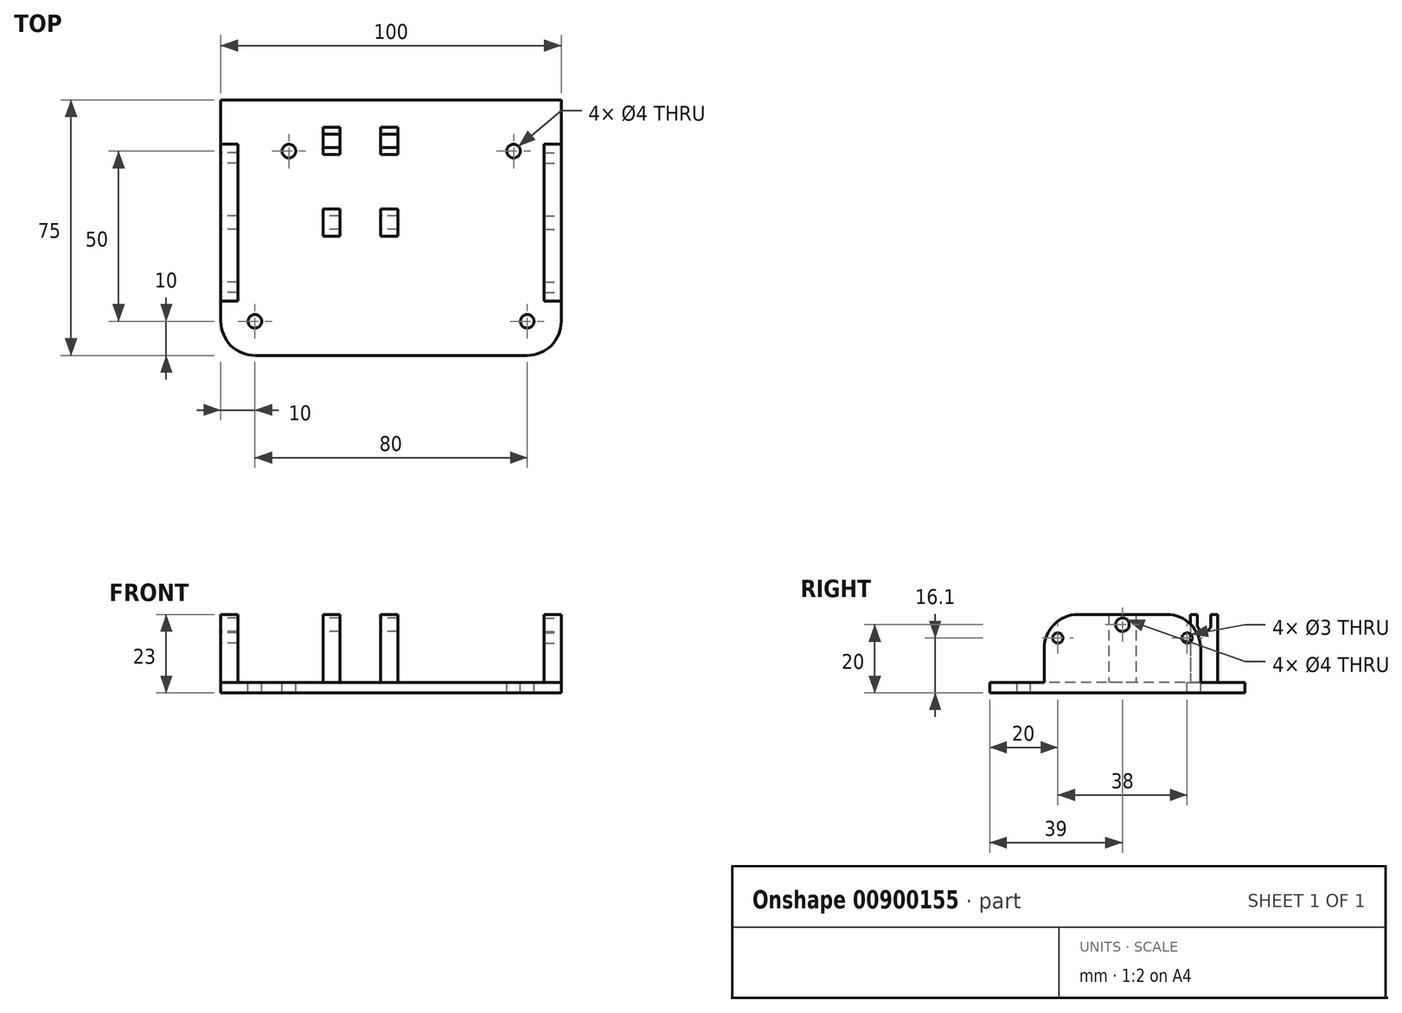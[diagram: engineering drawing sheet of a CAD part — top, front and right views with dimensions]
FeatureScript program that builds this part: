
annotation { "Feature Type Name" : "Feature", "Feature Type Description" : "" }
export const myFeature = defineFeature(function(context is Context, id is Id, definition is map)
    precondition{}
    {
        {
            var Q0;
            Q0=qCreatedBy(makeId("Top.planeOp"),FACE);
            var sketch = newSketch(context, id + "F0", { "sketchPlane" : qUnion([Q0])});
            skLineSegment(sketch, "E0.bottom", {"start": v(50, 37.5) * mm, "end": v(-50, 37.5) * mm});
            skLineSegment(sketch, "E0.top", {"start": v(40, -37.5) * mm, "end": v(-40, -37.5) * mm});
            skLineSegment(sketch, "E0.left", {"start": v(50, 37.5) * mm, "end": v(50, -27.5) * mm});
            skLineSegment(sketch, "E0.right", {"start": v(-50, 37.5) * mm, "end": v(-50, -27.5) * mm});
            skPoint(sketch, "E0.middle", {"position": v(0, 0) * mm});
            skPoint(sketch, "E1.visualSharp", {"position": v(50, -37.5) * mm});
            skArc(sketch, "E1.filletArc", {"start": v(40, -37.5) * mm, "mid": v(47.07, -34.57) * mm, "end": v(50, -27.5) * mm});
            skPoint(sketch, "E2.visualSharp", {"position": v(-50, -37.5) * mm});
            skArc(sketch, "E2.filletArc", {"start": v(-50, -27.5) * mm, "mid": v(-47.07, -34.57) * mm, "end": v(-40, -37.5) * mm});
            skSolve(sketch);
        }
        {
            var Q0;
            Q0 = qSketchRegion(id + "F0", true);
            extrude(context, id + "F1", {"entities" : qUnion([Q0]), "depth" : 3 * mm, "offsetDistance" : 25.4 * mm});
        }
        {
            var Q0;
            Q0=makeQuery(id+"F1.opExtrude","SWEPT_FACE",FACE,{"disambiguationData":[OSD([sQuery(id+"F0.wireOp",EDGE,"E0.left")])]});
            var sketch = newSketch(context, id + "F2", { "sketchPlane" : qUnion([Q0])});
            skLineSegment(sketch, "E3.bottom", {"start": v(-21.5, 3) * mm, "end": v(24.5, 3) * mm});
            skLineSegment(sketch, "E3.top", {"start": v(-11.5, 23) * mm, "end": v(14.5, 23) * mm});
            skLineSegment(sketch, "E3.left", {"start": v(-21.5, 3) * mm, "end": v(-21.5, 13) * mm});
            skLineSegment(sketch, "E3.right", {"start": v(24.5, 3) * mm, "end": v(24.5, 13) * mm});
            skCircle(sketch, "E4", {"center": v(1.5, 20) * mm, "radius": 2 * mm});
            skPoint(sketch, "E4.centerSnap0", {"position": v(1.5, 23) * mm});
            skCircle(sketch, "E5", {"center": v(-17.5, 16.1) * mm, "radius": 1.5 * mm});
            skCircle(sketch, "E6", {"center": v(20.5, 16.1) * mm, "radius": 1.5 * mm});
            skPoint(sketch, "E7.visualSharp", {"position": v(-21.5, 23) * mm});
            skArc(sketch, "E7.filletArc", {"start": v(-11.5, 23) * mm, "mid": v(-18.57, 20.07) * mm, "end": v(-21.5, 13) * mm});
            skPoint(sketch, "E8.visualSharp", {"position": v(24.5, 23) * mm});
            skArc(sketch, "E8.filletArc", {"start": v(24.5, 13) * mm, "mid": v(21.57, 20.07) * mm, "end": v(14.5, 23) * mm});
            skSolve(sketch);
        }
        {
            var Q0;
            Q0 = qSketchRegion(id + "F2", true);
            extrude(context, id + "F3", {"entities" : qUnion([Q0]), "operationType" : NewBodyOperationType.ADD, "oppositeDirection" : true, "depth" : 5 * mm, "offsetDistance" : 25.4 * mm});
        }
        {
            var Q0;
            Q0=makeQuery(id+"F1.opExtrude","SWEPT_FACE",FACE,{"disambiguationData":[OSD([sQuery(id+"F0.wireOp",EDGE,"E0.right")])]});
            var sketch = newSketch(context, id + "F4", { "sketchPlane" : qUnion([Q0])});
            skLineSegment(sketch, "E9.0", {"start": v(11.5, 23) * mm, "end": v(-14.5, 23) * mm});
            skArc(sketch, "E10.0", {"start": v(-24.5, 13) * mm, "mid": v(-21.57, 20.07) * mm, "end": v(-14.5, 23) * mm});
            skLineSegment(sketch, "E11.0.0", {"start": v(-24.5, 3) * mm, "end": v(21.5, 3) * mm});
            skLineSegment(sketch, "E11.0.1", {"start": v(21.5, 3) * mm, "end": v(21.5, 13) * mm});
            skArc(sketch, "E11.0.2", {"start": v(21.5, 13) * mm, "mid": v(18.57, 20.07) * mm, "end": v(11.5, 23) * mm});
            skArc(sketch, "E11.0.4", {"start": v(-14.5, 23) * mm, "mid": v(-21.57, 20.07) * mm, "end": v(-24.5, 13) * mm});
            skLineSegment(sketch, "E11.0.5", {"start": v(-24.5, 13) * mm, "end": v(-24.5, 3) * mm});
            skCircle(sketch, "E12.0", {"center": v(-20.5, 16.1) * mm, "radius": 1.5 * mm});
            skCircle(sketch, "E13.0", {"center": v(-1.5, 20) * mm, "radius": 2 * mm});
            skCircle(sketch, "E14.0", {"center": v(17.5, 16.1) * mm, "radius": 1.5 * mm});
            skSolve(sketch);
        }
        {
            var Q0;
            Q0 = qSketchRegion(id + "F4", true);
            extrude(context, id + "F5", {"entities" : qUnion([Q0]), "operationType" : NewBodyOperationType.ADD, "oppositeDirection" : true, "depth" : 5 * mm, "offsetDistance" : 25.4 * mm});
        }
        {
            var Q0;
            Q0=makeQuery(id+"F1.opExtrude","CAP_FACE",FACE,{"disambiguationData":[OSD([sQuery(id+"F0.wireOp",EDGE,"E0.bottom"),sQuery(id+"F0.wireOp",EDGE,"E0.top"),sQuery(id+"F0.wireOp",EDGE,"E0.left"),sQuery(id+"F0.wireOp",EDGE,"E0.right"),sQuery(id+"F0.wireOp",EDGE,"E1.filletArc"),sQuery(id+"F0.wireOp",EDGE,"E2.filletArc")])],"isStart":false});
            var sketch = newSketch(context, id + "F6", { "sketchPlane" : qUnion([Q0])});
            skCircle(sketch, "E15", {"center": v(-30, 22.5) * mm, "radius": 2 * mm});
            skCircle(sketch, "E16", {"center": v(36, 22.5) * mm, "radius": 2 * mm});
            skCircle(sketch, "E17", {"center": v(-40, -27.5) * mm, "radius": 2 * mm});
            skCircle(sketch, "E18", {"center": v(40, -27.5) * mm, "radius": 2 * mm});
            skLineSegment(sketch, "E19.0.0", {"start": v(-50, 24.5) * mm, "end": v(-45, 24.5) * mm});
            skLineSegment(sketch, "E19.0.1", {"start": v(-45, 24.5) * mm, "end": v(-45, -21.5) * mm});
            skLineSegment(sketch, "E19.0.2", {"start": v(-45, -21.5) * mm, "end": v(-50, -21.5) * mm});
            skLineSegment(sketch, "E19.0.3", {"start": v(-50, -21.5) * mm, "end": v(-50, -27.5) * mm});
            skArc(sketch, "E19.0.4", {"start": v(-50, -27.5) * mm, "mid": v(-47.07, -34.57) * mm, "end": v(-40, -37.5) * mm});
            skLineSegment(sketch, "E19.0.5", {"start": v(-40, -37.5) * mm, "end": v(40, -37.5) * mm});
            skArc(sketch, "E19.0.6", {"start": v(40, -37.5) * mm, "mid": v(47.07, -34.57) * mm, "end": v(50, -27.5) * mm});
            skLineSegment(sketch, "E19.0.7", {"start": v(50, -27.5) * mm, "end": v(50, -21.5) * mm});
            skLineSegment(sketch, "E19.0.8", {"start": v(50, -21.5) * mm, "end": v(45, -21.5) * mm});
            skLineSegment(sketch, "E19.0.9", {"start": v(45, -21.5) * mm, "end": v(45, 24.5) * mm});
            skLineSegment(sketch, "E19.0.10", {"start": v(45, 24.5) * mm, "end": v(50, 24.5) * mm});
            skLineSegment(sketch, "E19.0.11", {"start": v(50, 24.5) * mm, "end": v(50, 37.5) * mm});
            skLineSegment(sketch, "E19.0.12", {"start": v(50, 37.5) * mm, "end": v(-50, 37.5) * mm});
            skLineSegment(sketch, "E19.0.13", {"start": v(-50, 37.5) * mm, "end": v(-50, 24.5) * mm});
            skSolve(sketch);
        }
        {
            var Q0;
            Q0=makeQuery(id+"F6.imprint","IMPRINT",FACE,{"disambiguationData":[TD([[makeQuery(id+"F6.imprint","IMPRINT",EDGE,{"derivedFrom":sQuery(id+"F6.wireOp",EDGE,"E15")}),1.0]])]});
            var Q1;
            Q1=makeQuery(id+"F6.imprint","IMPRINT",FACE,{"disambiguationData":[TD([[makeQuery(id+"F6.imprint","IMPRINT",EDGE,{"derivedFrom":sQuery(id+"F6.wireOp",EDGE,"E17")}),1.0]])]});
            var Q2;
            Q2=makeQuery(id+"F6.imprint","IMPRINT",FACE,{"disambiguationData":[TD([[makeQuery(id+"F6.imprint","IMPRINT",EDGE,{"derivedFrom":sQuery(id+"F6.wireOp",EDGE,"E18")}),1.0]])]});
            var Q3;
            Q3=makeQuery(id+"F6.imprint","IMPRINT",FACE,{"disambiguationData":[TD([[makeQuery(id+"F6.imprint","IMPRINT",EDGE,{"derivedFrom":sQuery(id+"F6.wireOp",EDGE,"E16")}),1.0]])]});
            extrude(context, id + "F7", {"entities" : qUnion([Q0, Q1, Q2, Q3]), "operationType" : NewBodyOperationType.REMOVE, "oppositeDirection" : true, "depth" : 25.4 * mm, "offsetDistance" : 25.4 * mm});
        }
        {
            var Q0;
            Q0=makeQuery(id+"F1.opExtrude","CAP_FACE",FACE,{"disambiguationData":[OSD([sQuery(id+"F0.wireOp",EDGE,"E0.bottom"),sQuery(id+"F0.wireOp",EDGE,"E0.top"),sQuery(id+"F0.wireOp",EDGE,"E0.left"),sQuery(id+"F0.wireOp",EDGE,"E0.right"),sQuery(id+"F0.wireOp",EDGE,"E1.filletArc"),sQuery(id+"F0.wireOp",EDGE,"E2.filletArc")])],"isStart":false});
            var sketch = newSketch(context, id + "F8", { "sketchPlane" : qUnion([Q0])});
            skLineSegment(sketch, "E20.bottom", {"start": v(-20, 29.5) * mm, "end": v(-15, 29.5) * mm});
            skLineSegment(sketch, "E20.top", {"start": v(-20, 21.5) * mm, "end": v(-15, 21.5) * mm});
            skLineSegment(sketch, "E20.left", {"start": v(-20, 29.5) * mm, "end": v(-20, 21.5) * mm});
            skLineSegment(sketch, "E20.right", {"start": v(-15, 29.5) * mm, "end": v(-15, 21.5) * mm});
            skLineSegment(sketch, "E21.bottom", {"start": v(-3, 29.5) * mm, "end": v(2, 29.5) * mm});
            skLineSegment(sketch, "E21.top", {"start": v(-3, 21.5) * mm, "end": v(2, 21.5) * mm});
            skLineSegment(sketch, "E21.left", {"start": v(-3, 29.5) * mm, "end": v(-3, 21.5) * mm});
            skLineSegment(sketch, "E21.right", {"start": v(2, 29.5) * mm, "end": v(2, 21.5) * mm});
            skLineSegment(sketch, "E22.bottom", {"start": v(-20, 5.5) * mm, "end": v(-15, 5.5) * mm});
            skLineSegment(sketch, "E22.top", {"start": v(-20, -2.5) * mm, "end": v(-15, -2.5) * mm});
            skLineSegment(sketch, "E22.left", {"start": v(-20, 5.5) * mm, "end": v(-20, -2.5) * mm});
            skLineSegment(sketch, "E22.right", {"start": v(-15, 5.5) * mm, "end": v(-15, -2.5) * mm});
            skLineSegment(sketch, "E23.bottom", {"start": v(-3, 5.5) * mm, "end": v(2, 5.5) * mm});
            skLineSegment(sketch, "E23.top", {"start": v(-3, -2.5) * mm, "end": v(2, -2.5) * mm});
            skLineSegment(sketch, "E23.left", {"start": v(-3, 5.5) * mm, "end": v(-3, -2.5) * mm});
            skLineSegment(sketch, "E23.right", {"start": v(2, 5.5) * mm, "end": v(2, -2.5) * mm});
            skSolve(sketch);
        }
        {
            var Q0;
            Q0 = qSketchRegion(id + "F8", true);
            extrude(context, id + "F9", {"entities" : qUnion([Q0]), "operationType" : NewBodyOperationType.ADD, "depth" : 20 * mm, "offsetDistance" : 25.4 * mm});
        }
        {
            var Q0;
            Q0=makeQuery(id+"F9.opExtrude","SWEPT_FACE",FACE,{"disambiguationData":[OSD([sQuery(id+"F8.wireOp",EDGE,"E22.left")])]});
            var sketch = newSketch(context, id + "F10", { "sketchPlane" : qUnion([Q0])});
            skCircle(sketch, "E24.0", {"center": v(-1.5, 20) * mm, "radius": 2 * mm});
            skSolve(sketch);
        }
        {
            var Q0;
            Q0 = qSketchRegion(id + "F10", true);
            extrude(context, id + "F11", {"entities" : qUnion([Q0]), "operationType" : NewBodyOperationType.REMOVE, "oppositeDirection" : true, "depth" : 25.4 * mm, "offsetDistance" : 25.4 * mm});
        }
        {
            var Q0;
            Q0=makeQuery(id+"F9.opExtrude","SWEPT_FACE",FACE,{"disambiguationData":[OSD([sQuery(id+"F8.wireOp",EDGE,"E20.left")])]});
            var sketch = newSketch(context, id + "F12", { "sketchPlane" : qUnion([Q0])});
            skArc(sketch, "E25", {"start": v(-27.5, 20) * mm, "mid": v(-25.5, 18) * mm, "end": v(-23.5, 20) * mm});
            skLineSegment(sketch, "E26", {"start": v(-23.5, 20) * mm, "end": v(-23.5, 23) * mm});
            skLineSegment(sketch, "E27", {"start": v(-27.5, 20) * mm, "end": v(-27.5, 23) * mm});
            skLineSegment(sketch, "E28", {"start": v(-27.5, 23) * mm, "end": v(-23.5, 23) * mm});
            skSolve(sketch);
        }
        {
            var Q0;
            Q0 = qSketchRegion(id + "F12", true);
            extrude(context, id + "F13", {"entities" : qUnion([Q0]), "operationType" : NewBodyOperationType.REMOVE, "oppositeDirection" : true, "depth" : 25.4 * mm, "offsetDistance" : 25.4 * mm});
        }
    });
